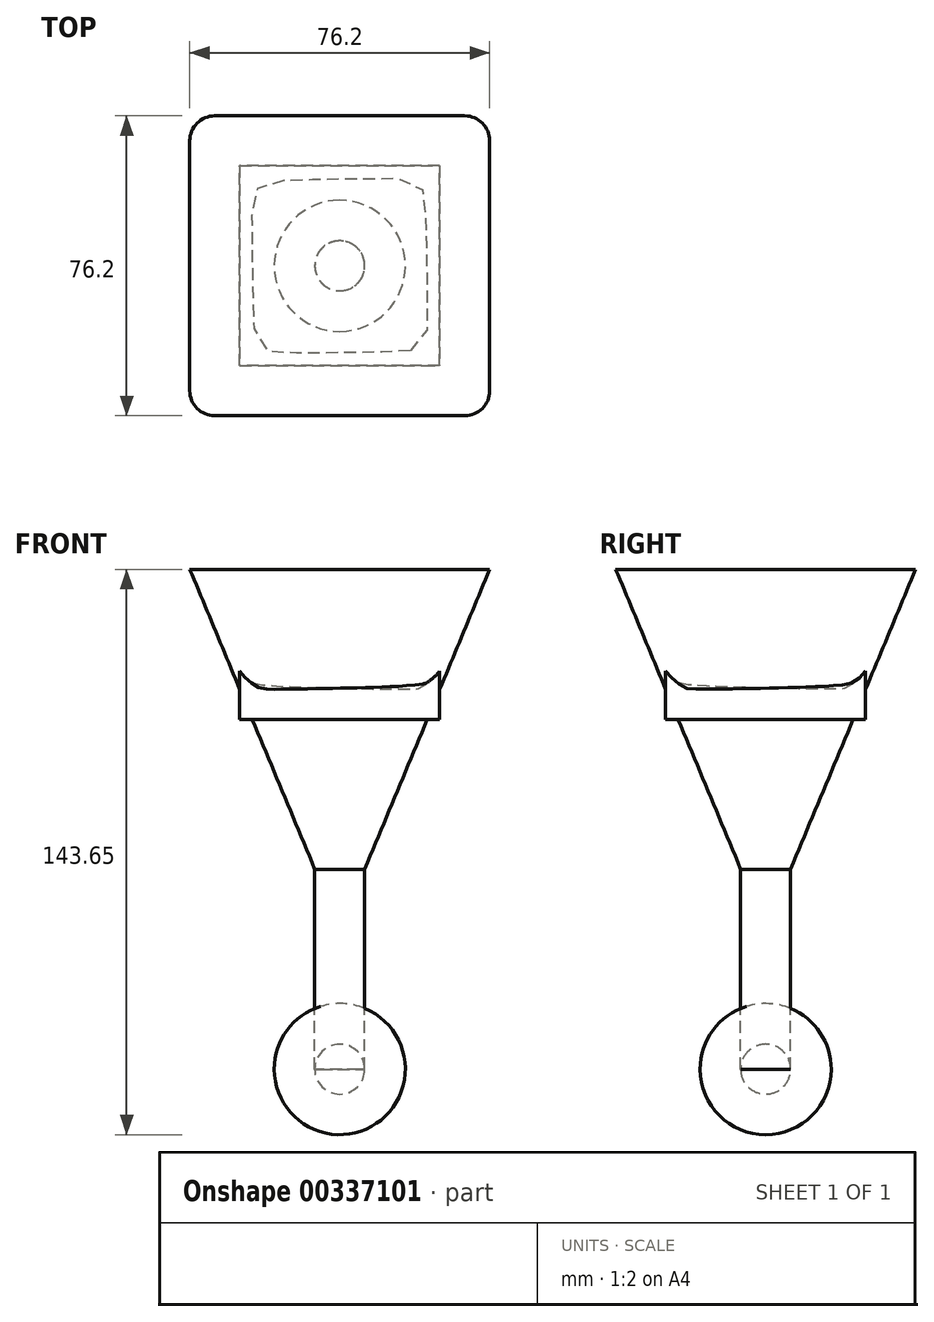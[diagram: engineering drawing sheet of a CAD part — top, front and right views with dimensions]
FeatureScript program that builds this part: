
annotation { "Feature Type Name" : "Feature", "Feature Type Description" : "" }
export const myFeature = defineFeature(function(context is Context, id is Id, definition is map)
    precondition{}
    {
        {
            var Q0;
            Q0=qCreatedBy(makeId("Top.planeOp"),FACE);
            var sketch = newSketch(context, id + "F0", { "sketchPlane" : qUnion([Q0])});
            skLineSegment(sketch, "E0.bottom", {"start": v(31.75, -38.1) * mm, "end": v(-31.75, -38.1) * mm});
            skLineSegment(sketch, "E0.top", {"start": v(31.75, 38.1) * mm, "end": v(-31.75, 38.1) * mm});
            skLineSegment(sketch, "E0.left", {"start": v(38.1, -31.75) * mm, "end": v(38.1, 31.75) * mm});
            skLineSegment(sketch, "E0.right", {"start": v(-38.1, -31.75) * mm, "end": v(-38.1, 31.75) * mm});
            skPoint(sketch, "E0.middle", {"position": v(0, 0) * mm});
            skPoint(sketch, "E1.visualSharp", {"position": v(38.1, -38.1) * mm});
            skArc(sketch, "E1.filletArc", {"start": v(31.75, -38.1) * mm, "mid": v(36.24, -36.24) * mm, "end": v(38.1, -31.75) * mm});
            skPoint(sketch, "E2.visualSharp", {"position": v(-38.1, -38.1) * mm});
            skArc(sketch, "E2.filletArc", {"start": v(-38.1, -31.75) * mm, "mid": v(-36.24, -36.24) * mm, "end": v(-31.75, -38.1) * mm});
            skPoint(sketch, "E3.visualSharp", {"position": v(-38.1, 38.1) * mm});
            skArc(sketch, "E3.filletArc", {"start": v(-31.75, 38.1) * mm, "mid": v(-36.24, 36.24) * mm, "end": v(-38.1, 31.75) * mm});
            skPoint(sketch, "E4.visualSharp", {"position": v(38.1, 38.1) * mm});
            skArc(sketch, "E4.filletArc", {"start": v(38.1, 31.75) * mm, "mid": v(36.24, 36.24) * mm, "end": v(31.75, 38.1) * mm});
            skSolve(sketch);
        }
        {
            var Q0;
            Q0=qCreatedBy(makeId("Top.planeOp"),FACE);
            cPlane(context, id + "F1", {"entities" : qUnion([Q0]), "cplaneType" : CPlaneType.OFFSET, "offset" : 76.2 * mm, "oppositeDirection" : true, "width" : 152.4 * mm, "height" : 152.4 * mm});
        }
        {
            var Q0;
            Q0=qCreatedBy(id+"F1.planeOp",FACE);
            var sketch = newSketch(context, id + "F2", { "sketchPlane" : qUnion([Q0])});
            skCircle(sketch, "E5", {"center": v(0, 0) * mm, "radius": 6.35 * mm});
            skSolve(sketch);
        }
        {
            var Q0;
            Q0=makeQuery(id+"F0.imprint","IMPRINT",FACE,{"disambiguationData":[TD([[makeQuery(id+"F0.imprint","IMPRINT",EDGE,{"derivedFrom":sQuery(id+"F0.wireOp",EDGE,"E0.bottom")}),-1.0]])]});
            var Q1;
            Q1=makeQuery(id+"F2.imprint","IMPRINT",FACE,{"disambiguationData":[TD([[makeQuery(id+"F2.imprint","IMPRINT",EDGE,{"derivedFrom":sQuery(id+"F2.wireOp",EDGE,"E5")}),1.0]])]});
            loft(context, id + "F3", {"sheetProfilesArray" : [{ "sheetProfileEntities" : qUnion([Q0]) }, { "sheetProfileEntities" : qUnion([Q1]) }]});
        }
        {
            var Q0;
            Q0=makeQuery(id+"F3.opLoft","CAP_FACE",FACE,{"disambiguationData":[OSD([makeQuery(id+"F2.imprint","IMPRINT",FACE,{"disambiguationData":[TD([[makeQuery(id+"F2.imprint","IMPRINT",EDGE,{"derivedFrom":sQuery(id+"F2.wireOp",EDGE,"E5")}),1.0]])]})])],"isStart":true});
            extrude(context, id + "F4", {"entities" : qUnion([Q0]), "operationType" : NewBodyOperationType.ADD, "depth" : 50.8 * mm});
        }
        {
            var Q0;
            Q0=makeQuery(id+"F4.opExtrude","CAP_FACE",FACE,{"disambiguationData":[OSD([makeQuery(id+"F2.imprint","IMPRINT",FACE,{"disambiguationData":[TD([[makeQuery(id+"F2.imprint","IMPRINT",EDGE,{"derivedFrom":sQuery(id+"F2.wireOp",EDGE,"E5")}),1.0]])]})])],"isStart":false});
            var sketch = newSketch(context, id + "F5", { "sketchPlane" : qUnion([Q0])});
            skArc(sketch, "E6", {"start": v(0, 16.65) * mm, "mid": v(-16.65, 0) * mm, "end": v(0, -16.65) * mm});
            skLineSegment(sketch, "E7", {"start": v(0, 16.65) * mm, "end": v(0, -16.65) * mm});
            skSolve(sketch);
        }
        {
            var Q0;
            {var subQ1=sQuery(id+"F5.wireOp",EDGE,"E6");Q0=makeQuery(id+"F5.imprint","IMPRINT",FACE,{"disambiguationData":[TD([[makeQuery(id+"F5.imprint","IMPRINT",EDGE,{"derivedFrom":subQ1}),1.0]])]});}
            var Q1;
            Q1=sQuery(id+"F5.wireOp",EDGE,"E7");
            revolve(context, id + "F6", {"entities" : qUnion([Q0]), "axis" : qUnion([Q1]), "revolveType" : RevolveType.FULL});
        }
        {
            var Q0;
            Q0=makeQuery(id+"F3.opLoft","CAP_FACE",FACE,{"disambiguationData":[OSD([makeQuery(id+"F0.imprint","IMPRINT",FACE,{"disambiguationData":[TD([[makeQuery(id+"F0.imprint","IMPRINT",EDGE,{"derivedFrom":sQuery(id+"F0.wireOp",EDGE,"E0.bottom")}),-1.0]])]})])],"isStart":true});
            var sketch = newSketch(context, id + "F7", { "sketchPlane" : qUnion([Q0])});
            skLineSegment(sketch, "E8.bottom", {"start": v(25.4, -25.4) * mm, "end": v(-25.4, -25.4) * mm});
            skLineSegment(sketch, "E8.top", {"start": v(25.4, 25.4) * mm, "end": v(-25.4, 25.4) * mm});
            skLineSegment(sketch, "E8.left", {"start": v(25.4, -25.4) * mm, "end": v(25.4, 25.4) * mm});
            skLineSegment(sketch, "E8.right", {"start": v(-25.4, -25.4) * mm, "end": v(-25.4, 25.4) * mm});
            skPoint(sketch, "E8.middle", {"position": v(0, 0) * mm});
            skSolve(sketch);
        }
        {
            var Q0;
            Q0=makeQuery(id+"F7.imprint","IMPRINT",FACE,{"disambiguationData":[TD([[makeQuery(id+"F7.imprint","IMPRINT",EDGE,{"derivedFrom":sQuery(id+"F7.wireOp",EDGE,"E8.bottom")}),-1.0]])]});
            extrude(context, id + "F8", {"entities" : qUnion([Q0]), "operationType" : NewBodyOperationType.ADD, "oppositeDirection" : true, "depth" : 38.1 * mm});
        }
    });
